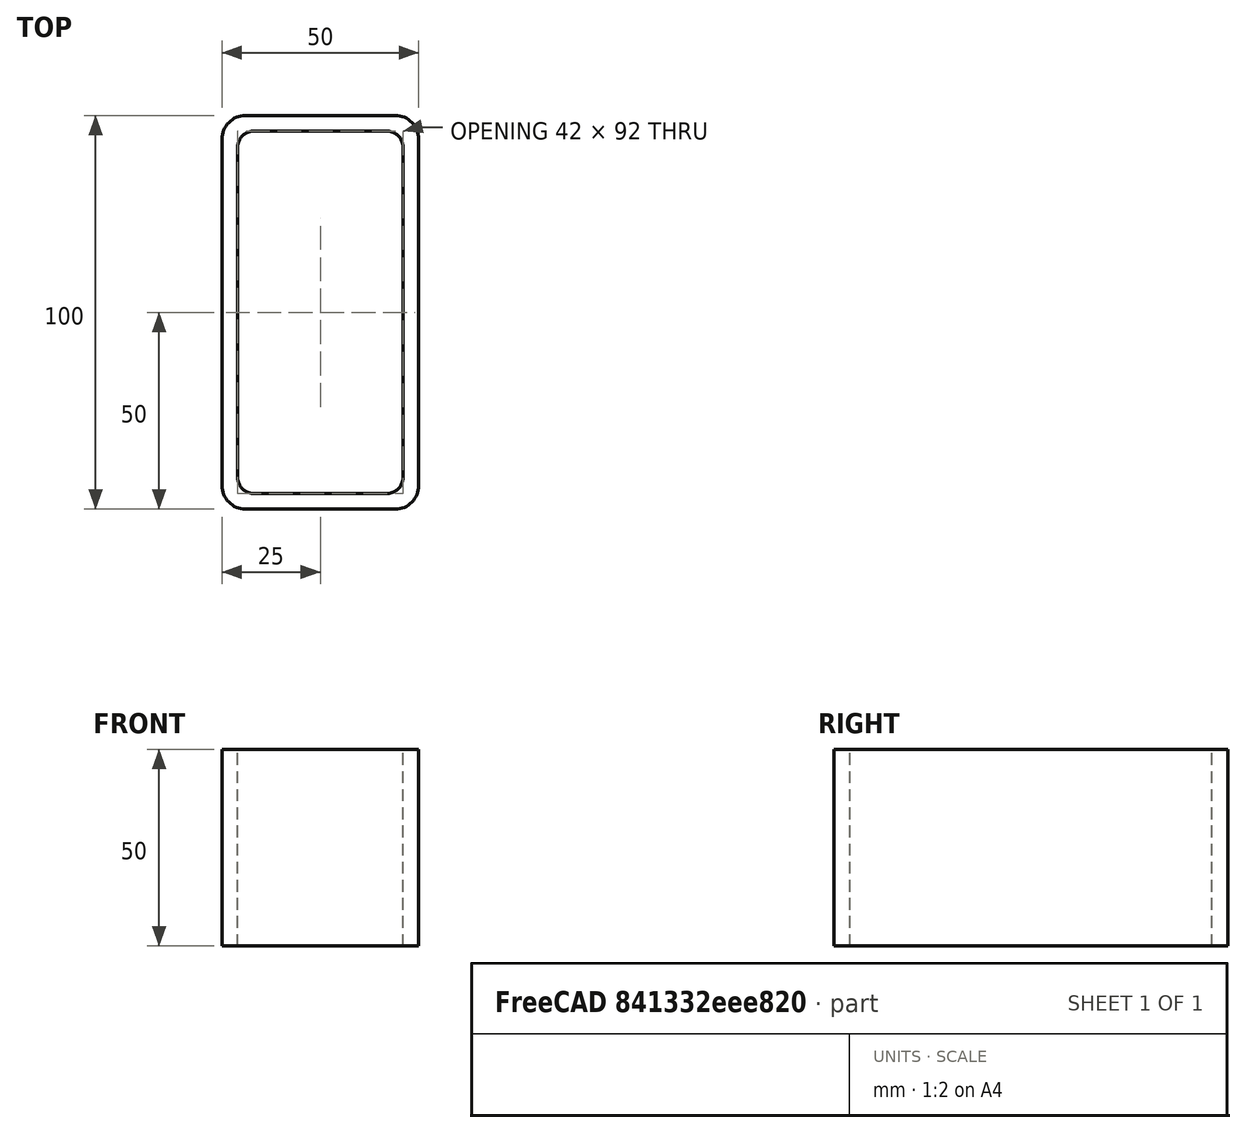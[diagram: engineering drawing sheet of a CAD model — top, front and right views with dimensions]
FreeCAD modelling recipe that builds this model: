
FCSTD DOCUMENT  (FreeCAD 0.15R4671 (Git))
Label: Rectangular hollow section 100x50x4 EN10219 S235JRH
License: All rights reserved
LicenseURL: http://en.wikipedia.org/wiki/All_rights_reserved
objects: Sketcher::SketchObject×1, Part::Extrusion×1
note: 2 computed .brp shape members not serialized (recipe doc carries the construction recipe); baked Part::Feature solids carry a one-line shape summary decoded from their .brp

FEATURE [Sketcher::SketchObject] Sketch
  sketch-geometry (16):
    g0: LineSegment StartX=-17 StartY=46 StartZ=0 EndX=17 EndY=46 EndZ=0
    g1: LineSegment StartX=21 StartY=42 StartZ=0 EndX=21 EndY=-42 EndZ=0
    g2: LineSegment StartX=17 StartY=-46 StartZ=0 EndX=-17 EndY=-46 EndZ=0
    g3: LineSegment StartX=-21 StartY=-42 StartZ=0 EndX=-21 EndY=42 EndZ=0
    g4: LineSegment StartX=-19 StartY=50 StartZ=0 EndX=19 EndY=50 EndZ=0
    g5: LineSegment StartX=25 StartY=44 StartZ=0 EndX=25 EndY=-44 EndZ=0
    g6: LineSegment StartX=19 StartY=-50 StartZ=0 EndX=-19 EndY=-50 EndZ=0
    g7: LineSegment StartX=-25 StartY=-44 StartZ=0 EndX=-25 EndY=44 EndZ=0
    g8: ArcOfCircle CenterX=-17 CenterY=42 CenterZ=0 NormalX=0 NormalY=0 NormalZ=1 Radius=4 StartAngle=1.5708 EndAngle=3.14159
    g9: ArcOfCircle CenterX=17 CenterY=42 CenterZ=0 NormalX=0 NormalY=0 NormalZ=1 Radius=4 StartAngle=0 EndAngle=1.5708
    g10: ArcOfCircle CenterX=17 CenterY=-42 CenterZ=0 NormalX=0 NormalY=0 NormalZ=1 Radius=4 StartAngle=4.71239 EndAngle=6.28319
    g11: ArcOfCircle CenterX=-17 CenterY=-42 CenterZ=0 NormalX=0 NormalY=0 NormalZ=1 Radius=4 StartAngle=3.14159 EndAngle=4.71239
    g12: ArcOfCircle CenterX=19 CenterY=44 CenterZ=0 NormalX=0 NormalY=0 NormalZ=1 Radius=6 StartAngle=0 EndAngle=1.5708
    g13: ArcOfCircle CenterX=19 CenterY=-44 CenterZ=0 NormalX=0 NormalY=0 NormalZ=1 Radius=6 StartAngle=4.71239 EndAngle=6.28319
    g14: ArcOfCircle CenterX=-19 CenterY=-44 CenterZ=0 NormalX=0 NormalY=0 NormalZ=1 Radius=6 StartAngle=3.14159 EndAngle=4.71239
    g15: ArcOfCircle CenterX=-19 CenterY=44 CenterZ=0 NormalX=0 NormalY=0 NormalZ=1 Radius=6 StartAngle=1.5708 EndAngle=3.14159
  constraints (36):
    c: Horizontal(g2)
    c: Vertical(g3)
    c: Horizontal(g6)
    c: Vertical(g7)
    c: Tangent(g3,g8) = 1.5708
    c: Tangent(g0,g8) = 1.5708
    c: Tangent(g0,g9) = 1.5708
    c: Tangent(g1,g9) = 1.5708
    c: Tangent(g1,g10) = 1.5708
    c: Tangent(g2,g10) = 1.5708
    c: Tangent(g2,g11) = 1.5708
    c: Tangent(g3,g11) = 1.5708
    c: Tangent(g4,g12) = 1.5708
    c: Tangent(g5,g12) = 1.5708
    c: Tangent(g5,g13) = 1.5708
    c: Tangent(g6,g13) = 1.5708
    c: Tangent(g6,g14) = 1.5708
    c: Tangent(g7,g14) = 1.5708
    c: Tangent(g7,g15) = 1.5708
    c: Tangent(g4,g15) = 1.5708
    c: Equal(g9,g8)
    c: Equal(g9,g11)
    c: Equal(g9,g10)
    c: Equal(g12,g15)
    c: Equal(g12,g14)
    c: Equal(g12,g13)
    c: Symmetric(g4,g6,g-1)
    c: Symmetric(g7,g5,g-2)
    c: DistanceY(g4,g6) = -100
    c: DistanceX(g7,g5) = 50
    c: Symmetric(g3,g1,g-2)
    c: Symmetric(g0,g2,g-1)
    c: DistanceY(g0,g4) = 4
    c: DistanceX(g5,g1) = -4
    c: Radius(g9) = 4
    c: Radius(g12) = 6
FEATURE [Part::Extrusion] Extrude  label="Rectangular hollow section 100x50x4 EN10219 S235JRH"
  Base = -> Sketch
  Dir = (0,0,50)
  Solid = true
